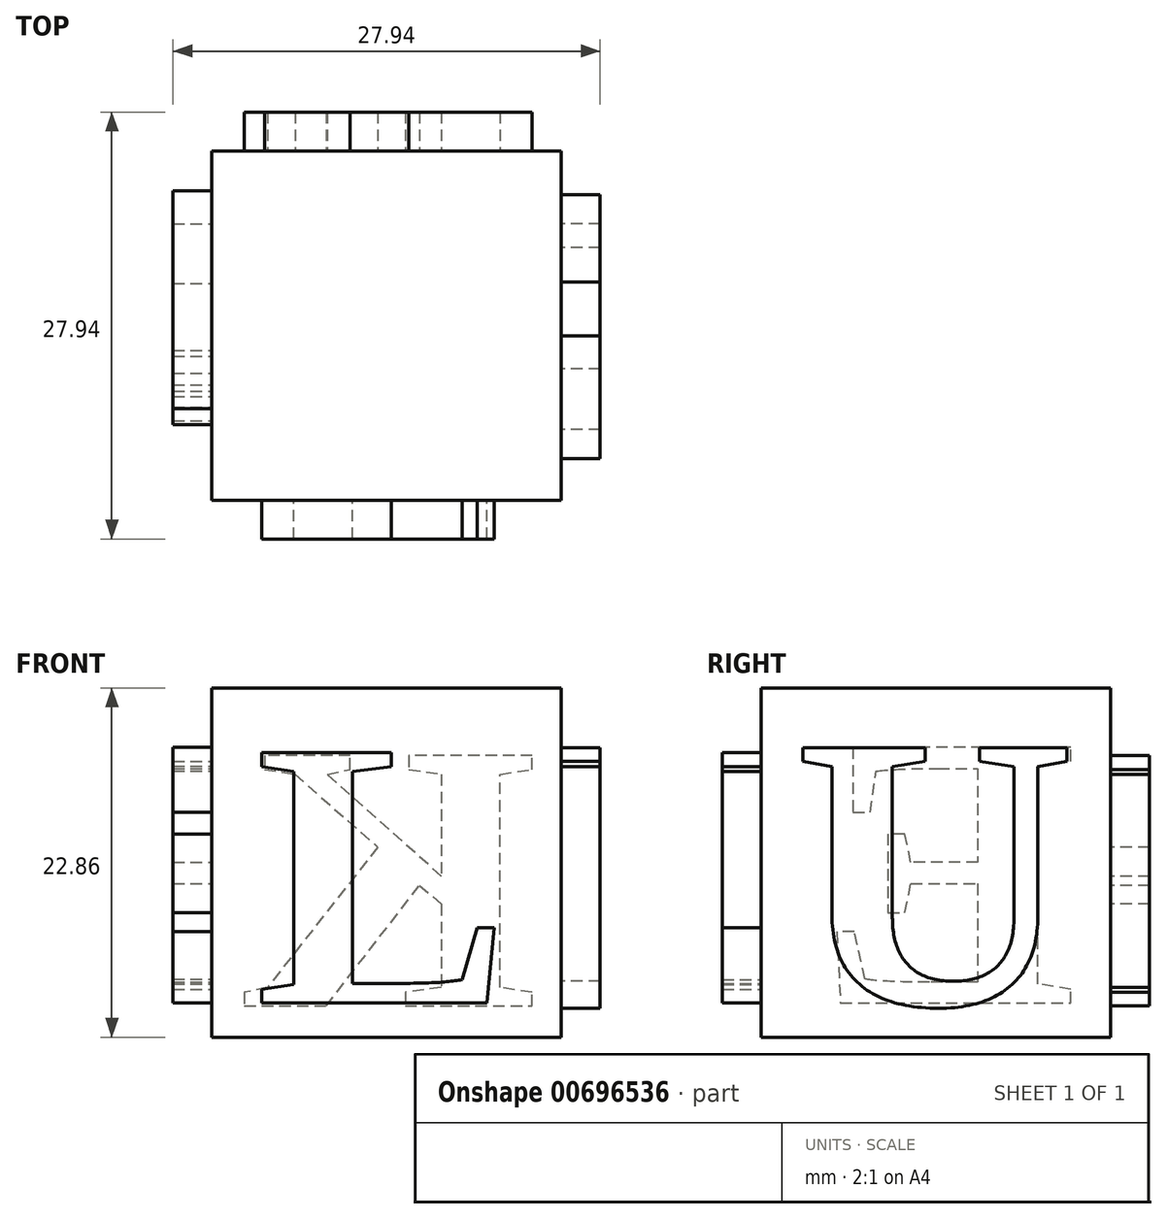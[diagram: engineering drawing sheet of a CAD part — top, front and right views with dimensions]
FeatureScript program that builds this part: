
annotation { "Feature Type Name" : "Feature", "Feature Type Description" : "" }
export const myFeature = defineFeature(function(context is Context, id is Id, definition is map)
    precondition{}
    {
        {
            var Q0;
            Q0=qCreatedBy(makeId("Front.planeOp"),FACE);
            var sketch = newSketch(context, id + "F0", { "sketchPlane" : qUnion([Q0])});
            skLineSegment(sketch, "E0.bottom", {"start": v(-11.43, 11.43) * mm, "end": v(11.43, 11.43) * mm});
            skLineSegment(sketch, "E0.top", {"start": v(-11.43, -11.43) * mm, "end": v(11.43, -11.43) * mm});
            skLineSegment(sketch, "E0.left", {"start": v(-11.43, 11.43) * mm, "end": v(-11.43, -11.43) * mm});
            skLineSegment(sketch, "E0.right", {"start": v(11.43, 11.43) * mm, "end": v(11.43, -11.43) * mm});
            skPoint(sketch, "E0.middle", {"position": v(0, 0) * mm});
            skSolve(sketch);
        }
        {
            var Q0;
            Q0 = qSketchRegion(id + "F0", true);
            extrude(context, id + "F1", {"entities" : qUnion([Q0]), "depth" : 22.86 * mm, "offsetDistance" : 25.4 * mm});
        }
        {
            var Q0;
            Q0=makeQuery(id+"F1.opExtrude","CAP_FACE",FACE,{"disambiguationData":[OSD([sQuery(id+"F0.wireOp",EDGE,"E0.bottom"),sQuery(id+"F0.wireOp",EDGE,"E0.top"),sQuery(id+"F0.wireOp",EDGE,"E0.left"),sQuery(id+"F0.wireOp",EDGE,"E0.right")])],"isStart":false});
            var sketch = newSketch(context, id + "F2", { "sketchPlane" : qUnion([Q0])});
            skText(sketch, "E1", { "text": "L", "fontName": "Tinos-Bold.ttf"});
            const initialGuessF2  = {"E1": [-0.0086, -0.0092, 1, 0, 0.01801]};
            skSetInitialGuess(sketch, initialGuessF2);
            skSolve(sketch);
        }
        {
            var Q0;
            Q0 = qSketchRegion(id + "F2", true);
            extrude(context, id + "F3", {"entities" : qUnion([Q0]), "operationType" : NewBodyOperationType.ADD, "depth" : 2.54 * mm, "offsetDistance" : 25.4 * mm});
        }
        {
            var Q0;
            Q0=makeQuery(id+"F1.opExtrude","SWEPT_FACE",FACE,{"disambiguationData":[OSD([sQuery(id+"F0.wireOp",EDGE,"E0.right")])]});
            var sketch = newSketch(context, id + "F4", { "sketchPlane" : qUnion([Q0])});
            skText(sketch, "E2", { "text": "U", "fontName": "Tinos-Bold.ttf"});
            const initialGuessF4  = {"E2": [-0.02078, -0.0093, 1, 0, 0.0185]};
            skSetInitialGuess(sketch, initialGuessF4);
            skSolve(sketch);
        }
        {
            var Q0;
            Q0 = qSketchRegion(id + "F4", true);
            extrude(context, id + "F5", {"entities" : qUnion([Q0]), "operationType" : NewBodyOperationType.ADD, "depth" : 2.54 * mm, "offsetDistance" : 25.4 * mm});
        }
        {
            var Q0;
            Q0=makeQuery(id+"F1.opExtrude","CAP_FACE",FACE,{"disambiguationData":[OSD([sQuery(id+"F0.wireOp",EDGE,"E0.bottom"),sQuery(id+"F0.wireOp",EDGE,"E0.top"),sQuery(id+"F0.wireOp",EDGE,"E0.left"),sQuery(id+"F0.wireOp",EDGE,"E0.right")])],"isStart":true});
            var sketch = newSketch(context, id + "F6", { "sketchPlane" : qUnion([Q0])});
            skText(sketch, "E3", { "text": "K", "fontName": "Tinos-Bold.ttf"});
            const initialGuessF6  = {"E3": [-0.00995, -0.00939, 1, 0, 0.01801]};
            skSetInitialGuess(sketch, initialGuessF6);
            skSolve(sketch);
        }
        {
            var Q0;
            Q0 = qSketchRegion(id + "F6", true);
            extrude(context, id + "F7", {"entities" : qUnion([Q0]), "operationType" : NewBodyOperationType.ADD, "depth" : 2.54 * mm, "offsetDistance" : 25.4 * mm});
        }
        {
            var Q0;
            Q0=makeQuery(id+"F1.opExtrude","SWEPT_FACE",FACE,{"disambiguationData":[OSD([sQuery(id+"F0.wireOp",EDGE,"E0.left")])]});
            var sketch = newSketch(context, id + "F8", { "sketchPlane" : qUnion([Q0])});
            skText(sketch, "E4", { "text": "E", "fontName": "Tinos-Bold.ttf"});
            const initialGuessF8  = {"E4": [0.00218, -0.0092, 1, 0, 0.0184]};
            skSetInitialGuess(sketch, initialGuessF8);
            skSolve(sketch);
        }
        {
            var Q0;
            Q0 = qSketchRegion(id + "F8", true);
            extrude(context, id + "F9", {"entities" : qUnion([Q0]), "operationType" : NewBodyOperationType.ADD, "depth" : 2.54 * mm, "offsetDistance" : 25.4 * mm});
        }
    });
